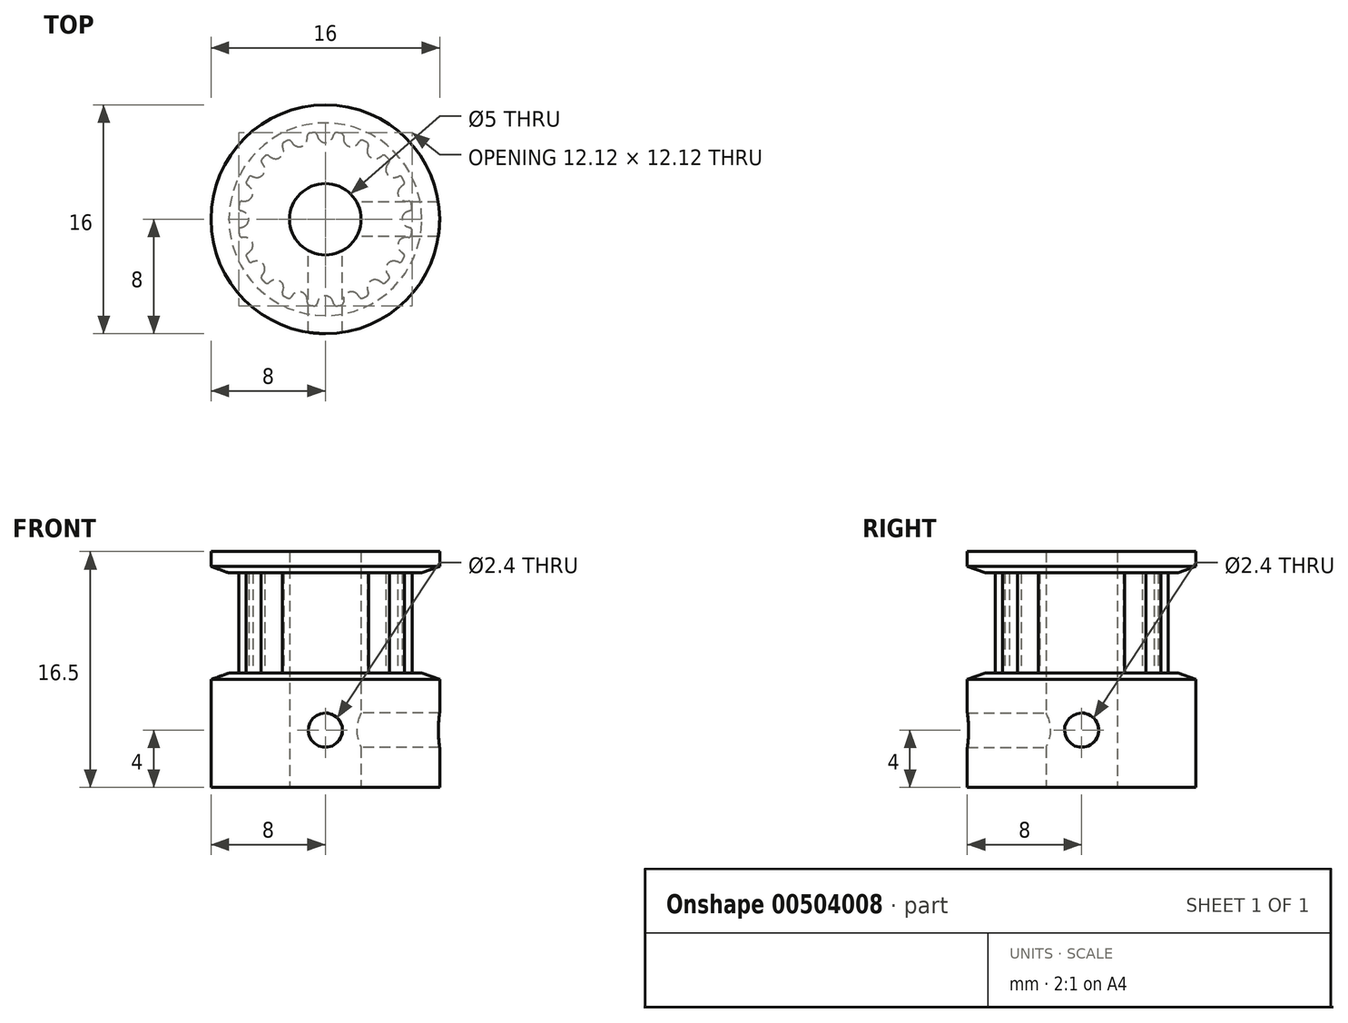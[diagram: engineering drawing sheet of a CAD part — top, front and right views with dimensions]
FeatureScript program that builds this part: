
annotation { "Feature Type Name" : "Feature", "Feature Type Description" : "" }
export const myFeature = defineFeature(function(context is Context, id is Id, definition is map)
    precondition{}
    {
        {
            assignVariable(context, id + "F0", {"name" : "teeth", "anyValue" : 20});
        }
        {
            assignVariable(context, id + "F1", {"name" : "belt_width", "anyValue" : 6 * mm});
        }
        {
            assignVariable(context, id + "F2", {"name" : "bore_diameter", "anyValue" : 5 * mm});
        }
        {
            var Q0;
            Q0=qCreatedBy(makeId("Top.planeOp"),FACE);
            var sketch = newSketch(context, id + "F3", { "sketchPlane" : qUnion([Q0])});
            skLineSegment(sketch, "E0", {"start": v(0, 0) * mm, "end": v(0, 5.36) * mm, "construction": true});
            skCircle(sketch, "E1", {"center": v(0, 0) * mm, "radius": 6.11 * mm});
            skPoint(sketch, "E2.MirrorCS.end.orphan", {"position": v(0.96, 6.04) * mm});
            skLineSegment(sketch, "E3", {"start": v(0.96, 6.04) * mm, "end": v(1, 6.29) * mm, "construction": true});
            skLineSegment(sketch, "E4", {"start": v(-0.96, 6.04) * mm, "end": v(-1, 6.29) * mm, "construction": true});
            skArc(sketch, "E5", {"start": v(0, 5.36) * mm, "mid": v(0.31, 5.46) * mm, "end": v(0.52, 5.72) * mm});
            skArc(sketch, "E6", {"start": v(0.52, 5.72) * mm, "mid": v(0.56, 5.83) * mm, "end": v(0.58, 5.94) * mm, "construction": true});
            skLineSegment(sketch, "E7", {"start": v(0, 5.36) * mm, "end": v(0, 6.11) * mm, "construction": true});
            skLineSegment(sketch, "E8", {"start": v(0, 6.11) * mm, "end": v(0, 6.37) * mm, "construction": true});
            skArc(sketch, "E9", {"start": v(0.58, 5.94) * mm, "mid": v(0.64, 6.04) * mm, "end": v(0.75, 6.07) * mm, "construction": true});
            skArc(sketch, "E10", {"start": v(1, 6.29) * mm, "mid": v(0, 6.37) * mm, "end": v(-1, 6.29) * mm, "construction": true});
            skLineSegment(sketch, "E11", {"start": v(0.96, 6.04) * mm, "end": v(0.84, 5.3) * mm});
            skLineSegment(sketch, "E12", {"start": v(0.84, 5.3) * mm, "end": v(0, 0) * mm});
            skLineSegment(sketch, "E13", {"start": v(0, 0) * mm, "end": v(-0.84, 5.3) * mm});
            skLineSegment(sketch, "E14", {"start": v(-0.84, 5.3) * mm, "end": v(-0.96, 6.04) * mm});
            skArc(sketch, "E15", {"start": v(0.8, 6.06) * mm, "mid": v(0.67, 6.03) * mm, "end": v(0.6, 5.93) * mm});
            skArc(sketch, "E16", {"start": v(0.52, 5.72) * mm, "mid": v(0.56, 5.83) * mm, "end": v(0.6, 5.93) * mm});
            skArc(sketch, "E17.MirrorCS", {"start": v(0, 5.36) * mm, "mid": v(-0.31, 5.46) * mm, "end": v(-0.52, 5.72) * mm});
            skArc(sketch, "E18.MirrorCS", {"start": v(-0.52, 5.72) * mm, "mid": v(-0.56, 5.83) * mm, "end": v(-0.6, 5.93) * mm});
            skArc(sketch, "E19.MirrorCS", {"start": v(-0.8, 6.06) * mm, "mid": v(-0.67, 6.03) * mm, "end": v(-0.6, 5.93) * mm});
            skArc(sketch, "E20", {"start": v(0, 6.11) * mm, "mid": v(-0.2, 6.1) * mm, "end": v(-0.4, 6.1) * mm});
            skArc(sketch, "E21", {"start": v(0.84, 5.3) * mm, "mid": v(0, 5.36) * mm, "end": v(-0.84, 5.3) * mm, "construction": true});
            skLineSegment(sketch, "E22", {"start": v(1, 6.29) * mm, "end": v(1.05, 6.66) * mm, "construction": true});
            skLineSegment(sketch, "E23", {"start": v(-1, 6.29) * mm, "end": v(-1.05, 6.66) * mm, "construction": true});
            skArc(sketch, "E24", {"start": v(-1.05, 6.66) * mm, "mid": v(0, 6.74) * mm, "end": v(1.05, 6.66) * mm, "construction": true});
            skSolve(sketch);
        }
        {
            var Q0;
            Q0=makeQuery(id+"F3.imprint","IMPRINT",FACE,{"disambiguationData":[TD([[makeQuery(id+"F3.imprint","IMPRINT",EDGE,{"derivedFrom":sQuery(id+"F3.wireOp",EDGE,"E5")}),-1.0]])]});
            var Q1;
            {var subQ1=sQuery(id+"F3.wireOp",EDGE,"E14");Q1=makeQuery(id+"F3.imprint","IMPRINT",FACE,{"disambiguationData":[TD([[makeQuery(id+"F3.imprint","IMPRINT",EDGE,{"derivedFrom":subQ1}),-1.0]])]});}
            var Q2;
            {var subQ0=sQuery(id+"F3.wireOp",EDGE,"E12");Q2=makeQuery(id+"F3.imprint","IMPRINT",FACE,{"disambiguationData":[TD([[makeQuery(id+"F3.imprint","IMPRINT",EDGE,{"derivedFrom":subQ0}),-1.0]])]});}
            extrude(context, id + "F4", {"entities" : qUnion([Q0, Q1, Q2]), "depth" : (getVariable(context, 'belt_width')) + 1 * mm, "offsetDistance" : 25 * mm, "symmetric" : true});
        }
        {
            var Q0;
            Q0=makeQuery(id+"F4.opExtrude","SWEPT_BODY",BODY,{"disambiguationData":[OSD([sQuery(id+"F3.wireOp",EDGE,"E1"),sQuery(id+"F3.wireOp",EDGE,"E5"),sQuery(id+"F3.wireOp",EDGE,"E11"),sQuery(id+"F3.wireOp",EDGE,"E12"),sQuery(id+"F3.wireOp",EDGE,"E13"),sQuery(id+"F3.wireOp",EDGE,"E14"),sQuery(id+"F3.wireOp",EDGE,"E15"),sQuery(id+"F3.wireOp",EDGE,"E16"),sQuery(id+"F3.wireOp",EDGE,"E17.MirrorCS"),sQuery(id+"F3.wireOp",EDGE,"E18.MirrorCS"),sQuery(id+"F3.wireOp",EDGE,"E19.MirrorCS")])]});
            var Q1;
            Q1=makeQuery(id+"F4.opExtrude","SWEPT_EDGE",EDGE,{"disambiguationData":[OSD([sQuery(id+"F3.wireOp",EDGE,"E12"),sQuery(id+"F3.wireOp",EDGE,"E13")])]});
            circularPattern(context, id + "F5", {"operationType" : NewBodyOperationType.ADD, "entities" : qUnion([Q0]), "axis" : qUnion([Q1]), "angle" : 360 * degree, "instanceCount" : getVariable(context, 'teeth'), "equalSpace" : true});
        }
        {
            var Q0;
            Q0=qCreatedBy(makeId("Front.planeOp"),FACE);
            var sketch = newSketch(context, id + "F6", { "sketchPlane" : qUnion([Q0])});
            skLineSegment(sketch, "E25", {"start": v(0, -3.5) * mm, "end": v(6.74, -3.5) * mm});
            skLineSegment(sketch, "E26", {"start": v(6.74, -3.5) * mm, "end": v(8, -3.96) * mm});
            skLineSegment(sketch, "E27", {"start": v(8, -3.96) * mm, "end": v(8, -11.5) * mm});
            skLineSegment(sketch, "E28", {"start": v(8, -11.5) * mm, "end": v(0, -11.5) * mm});
            skLineSegment(sketch, "E29", {"start": v(0, -11.5) * mm, "end": v(0, -3.5) * mm});
            skLineSegment(sketch, "E30", {"start": v(0, 3.5) * mm, "end": v(6.74, 3.5) * mm});
            skLineSegment(sketch, "E31", {"start": v(8, 3.96) * mm, "end": v(6.74, 3.5) * mm});
            skLineSegment(sketch, "E32", {"start": v(8, 3.96) * mm, "end": v(8, 5) * mm});
            skLineSegment(sketch, "E33", {"start": v(8, 5) * mm, "end": v(0, 5) * mm});
            skLineSegment(sketch, "E34", {"start": v(0, 5) * mm, "end": v(0, 3.5) * mm});
            skLineSegment(sketch, "E35", {"start": v(6.74, -3.5) * mm, "end": v(8, -3.5) * mm, "construction": true});
            skLineSegment(sketch, "E36", {"start": v(8, -3.5) * mm, "end": v(8, -3.96) * mm, "construction": true});
            skLineSegment(sketch, "E37", {"start": v(6.74, 3.5) * mm, "end": v(8, 3.5) * mm, "construction": true});
            skLineSegment(sketch, "E38", {"start": v(8, 3.5) * mm, "end": v(8, 3.96) * mm, "construction": true});
            skLineSegment(sketch, "E39", {"start": v(6.11, 0) * mm, "end": v(6.11, -3.5) * mm, "construction": true});
            skSolve(sketch);
        }
        {
            var Q0;
            Q0=qSketchRegion(id+"F6",true);
            var Q1;
            Q1=qConstructionFilter(qBodyType(qCreatedBy(id+"F6",EDGE),BodyType.WIRE),ConstructionObject.NO);
            var Q2;
            Q2=sQuery(id+"F6.wireOp",EDGE,"E29");
            revolve(context, id + "F7", {"operationType" : NewBodyOperationType.ADD, "entities" : qUnion([Q0]), "surfaceEntities" : qUnion([Q1]), "axis" : qUnion([Q2]), "revolveType" : RevolveType.FULL});
        }
        {
            var Q0;
            Q0=makeQuery(id+"F7.opRevolve","SWEPT_FACE",FACE,{"disambiguationData":[OSD([sQuery(id+"F6.wireOp",EDGE,"E28")])]});
            var sketch = newSketch(context, id + "F8", { "sketchPlane" : qUnion([Q0])});
            skPoint(sketch, "E40", {"position": v(0, 0) * mm});
            skSolve(sketch);
        }
        {
            var Q0;
            Q0=sQuery(id+"F8.wireOp",VERTEX,"E40");
            var Q1;
            Q1=makeQuery(id+"F4.opExtrude","SWEPT_BODY",BODY,{"disambiguationData":[OSD([sQuery(id+"F3.wireOp",EDGE,"E1"),sQuery(id+"F3.wireOp",EDGE,"E5"),sQuery(id+"F3.wireOp",EDGE,"E11"),sQuery(id+"F3.wireOp",EDGE,"E12"),sQuery(id+"F3.wireOp",EDGE,"E13"),sQuery(id+"F3.wireOp",EDGE,"E14"),sQuery(id+"F3.wireOp",EDGE,"E15"),sQuery(id+"F3.wireOp",EDGE,"E16"),sQuery(id+"F3.wireOp",EDGE,"E17.MirrorCS"),sQuery(id+"F3.wireOp",EDGE,"E18.MirrorCS"),sQuery(id+"F3.wireOp",EDGE,"E19.MirrorCS")])]});
            hole(context, id + "F9", {"style" : HoleStyle.SIMPLE, "holeDiameter" : getVariable(context, 'bore_diameter'), "endStyle" : HoleEndStyle.THROUGH, "locations" : qUnion([Q0]), "scope" : qUnion([Q1]), "isTappedThrough" : true});
        }
        {
            var Q0;
            Q0=qCreatedBy(makeId("Front.planeOp"),FACE);
            var sketch = newSketch(context, id + "F10", { "sketchPlane" : qUnion([Q0])});
            skPoint(sketch, "E41", {"position": v(0, -7.5) * mm});
            skLineSegment(sketch, "E42", {"start": v(0, -11.5) * mm, "end": v(0, -3.5) * mm});
            skSolve(sketch);
        }
        {
            var Q0;
            Q0=qCreatedBy(makeId("Right.planeOp"),FACE);
            var sketch = newSketch(context, id + "F11", { "sketchPlane" : qUnion([Q0])});
            skPoint(sketch, "E43", {"position": v(0, -7.5) * mm});
            skSolve(sketch);
        }
        {
            var Q0;
            Q0=sQuery(id+"F10.wireOp",VERTEX,"E41");
            var Q1;
            Q1=makeQuery(id+"F4.opExtrude","SWEPT_BODY",BODY,{"disambiguationData":[OSD([sQuery(id+"F3.wireOp",EDGE,"E1"),sQuery(id+"F3.wireOp",EDGE,"E5"),sQuery(id+"F3.wireOp",EDGE,"E11"),sQuery(id+"F3.wireOp",EDGE,"E12"),sQuery(id+"F3.wireOp",EDGE,"E13"),sQuery(id+"F3.wireOp",EDGE,"E14"),sQuery(id+"F3.wireOp",EDGE,"E15"),sQuery(id+"F3.wireOp",EDGE,"E16"),sQuery(id+"F3.wireOp",EDGE,"E17.MirrorCS"),sQuery(id+"F3.wireOp",EDGE,"E18.MirrorCS"),sQuery(id+"F3.wireOp",EDGE,"E19.MirrorCS")])]});
            hole(context, id + "F12", {"style" : HoleStyle.SIMPLE, "endStyle" : HoleEndStyle.THROUGH, "oppositeDirection" : true, "standardTappedOrClearance" : lookupTablePath({ "standard" : "ISO", "engagement" : "75%", "pitch" : "0.6 mm", "size" : "M3", "type" : "Tapped" }), "standardBlindInLast" : lookupTablePath({ "standard" : "ISO", "engagement" : "75%", "pitch" : "0.6 mm", "size" : "M3", "type" : "Tapped" }), "holeDiameter" : 2.4 * mm, "locations" : qUnion([Q0]), "scope" : qUnion([Q1]), "isTappedThrough" : true, "showTappedDepth" : true});
        }
        {
            var Q0;
            Q0=sQuery(id+"F11.wireOp",VERTEX,"E43");
            var Q1;
            Q1=makeQuery(id+"F4.opExtrude","SWEPT_BODY",BODY,{"disambiguationData":[OSD([sQuery(id+"F3.wireOp",EDGE,"E1"),sQuery(id+"F3.wireOp",EDGE,"E5"),sQuery(id+"F3.wireOp",EDGE,"E11"),sQuery(id+"F3.wireOp",EDGE,"E12"),sQuery(id+"F3.wireOp",EDGE,"E13"),sQuery(id+"F3.wireOp",EDGE,"E14"),sQuery(id+"F3.wireOp",EDGE,"E15"),sQuery(id+"F3.wireOp",EDGE,"E16"),sQuery(id+"F3.wireOp",EDGE,"E17.MirrorCS"),sQuery(id+"F3.wireOp",EDGE,"E18.MirrorCS"),sQuery(id+"F3.wireOp",EDGE,"E19.MirrorCS")])]});
            hole(context, id + "F13", {"style" : HoleStyle.SIMPLE, "endStyle" : HoleEndStyle.THROUGH, "oppositeDirection" : true, "standardTappedOrClearance" : lookupTablePath({ "standard" : "ISO", "engagement" : "75%", "pitch" : "0.6 mm", "size" : "M3", "type" : "Tapped" }), "standardBlindInLast" : lookupTablePath({ "standard" : "ISO", "engagement" : "75%", "pitch" : "0.6 mm", "size" : "M3", "type" : "Tapped" }), "holeDiameter" : 2.4 * mm, "locations" : qUnion([Q0]), "scope" : qUnion([Q1]), "isTappedThrough" : true, "showTappedDepth" : true});
        }
    });
